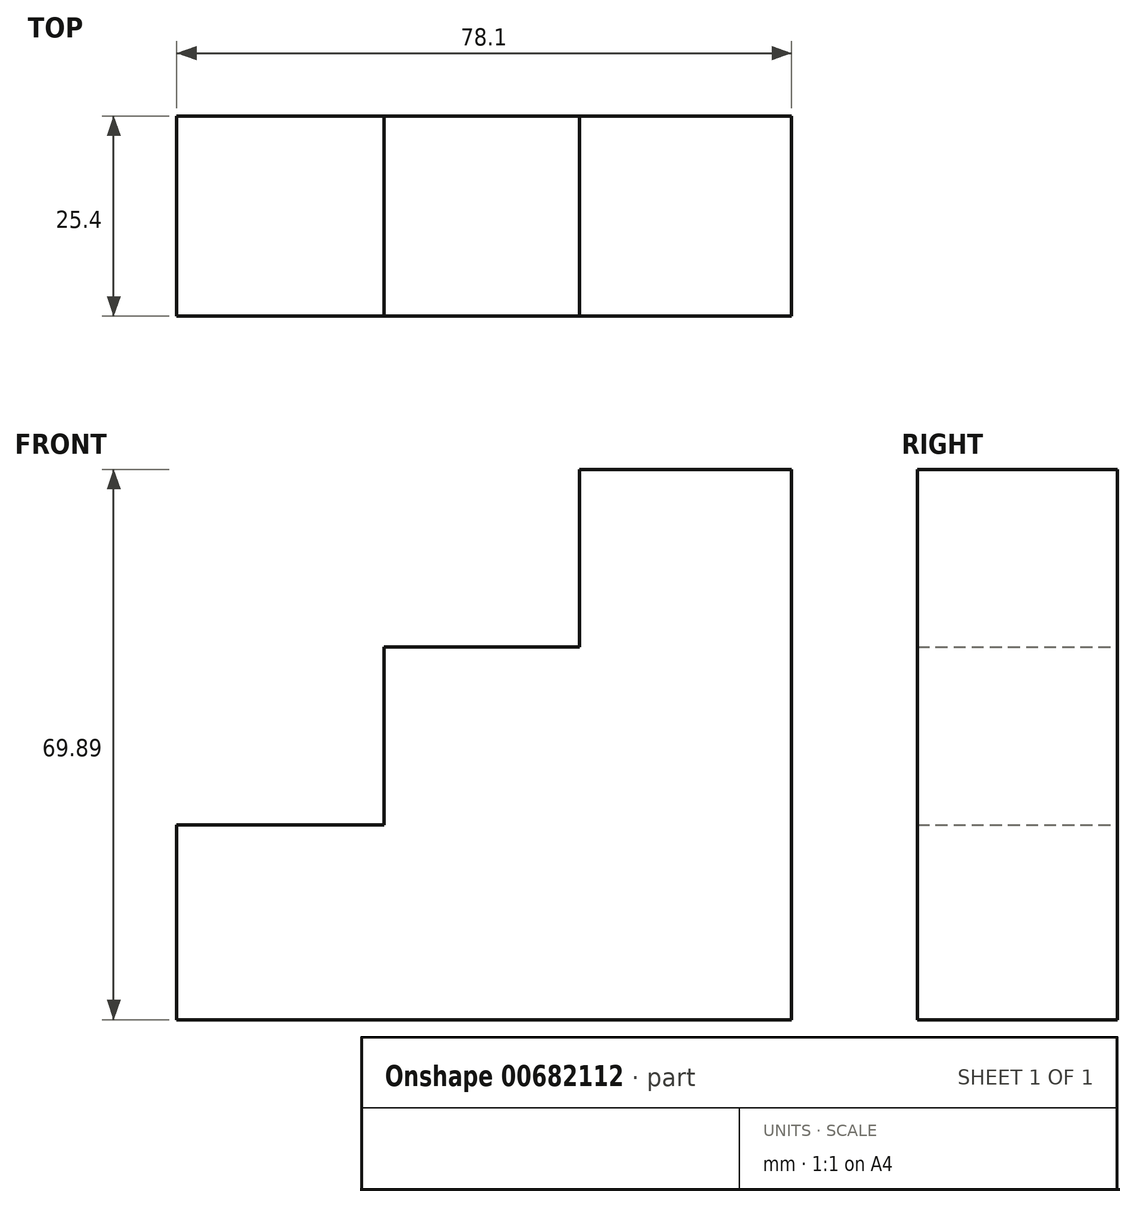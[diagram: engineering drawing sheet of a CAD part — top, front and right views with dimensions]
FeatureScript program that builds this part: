
annotation { "Feature Type Name" : "Feature", "Feature Type Description" : "" }
export const myFeature = defineFeature(function(context is Context, id is Id, definition is map)
    precondition{}
    {
        {
            var Q0;
            Q0=qCreatedBy(makeId("Front.planeOp"),FACE);
            var sketch = newSketch(context, id + "F0", { "sketchPlane" : qUnion([Q0])});
            skLineSegment(sketch, "E0", {"start": v(-59.3, 0) * mm, "end": v(-32.94, 0) * mm});
            skLineSegment(sketch, "E1", {"start": v(-32.94, 0) * mm, "end": v(-32.94, 22.63) * mm});
            skLineSegment(sketch, "E2", {"start": v(-32.94, 22.63) * mm, "end": v(-8.12, 22.63) * mm});
            skLineSegment(sketch, "E3", {"start": v(-8.12, 22.63) * mm, "end": v(-8.12, 45.16) * mm});
            skLineSegment(sketch, "E4", {"start": v(-8.12, 45.16) * mm, "end": v(18.8, 45.16) * mm});
            skLineSegment(sketch, "E5", {"start": v(18.8, 45.16) * mm, "end": v(18.8, -24.73) * mm});
            skLineSegment(sketch, "E6", {"start": v(-59.3, -24.73) * mm, "end": v(18.8, -24.73) * mm});
            skPoint(sketch, "E7.start.orphan", {"position": v(-59.3, -22.82) * mm});
            skLineSegment(sketch, "E8", {"start": v(-59.3, -24.73) * mm, "end": v(-59.3, 0) * mm});
            skSolve(sketch);
        }
        {
            var Q0;
            Q0 = qSketchRegion(id + "F0", true);
            extrude(context, id + "F1", {"entities" : qUnion([Q0]), "depth" : 25.4 * mm, "offsetDistance" : 25.4 * mm});
        }
    });
